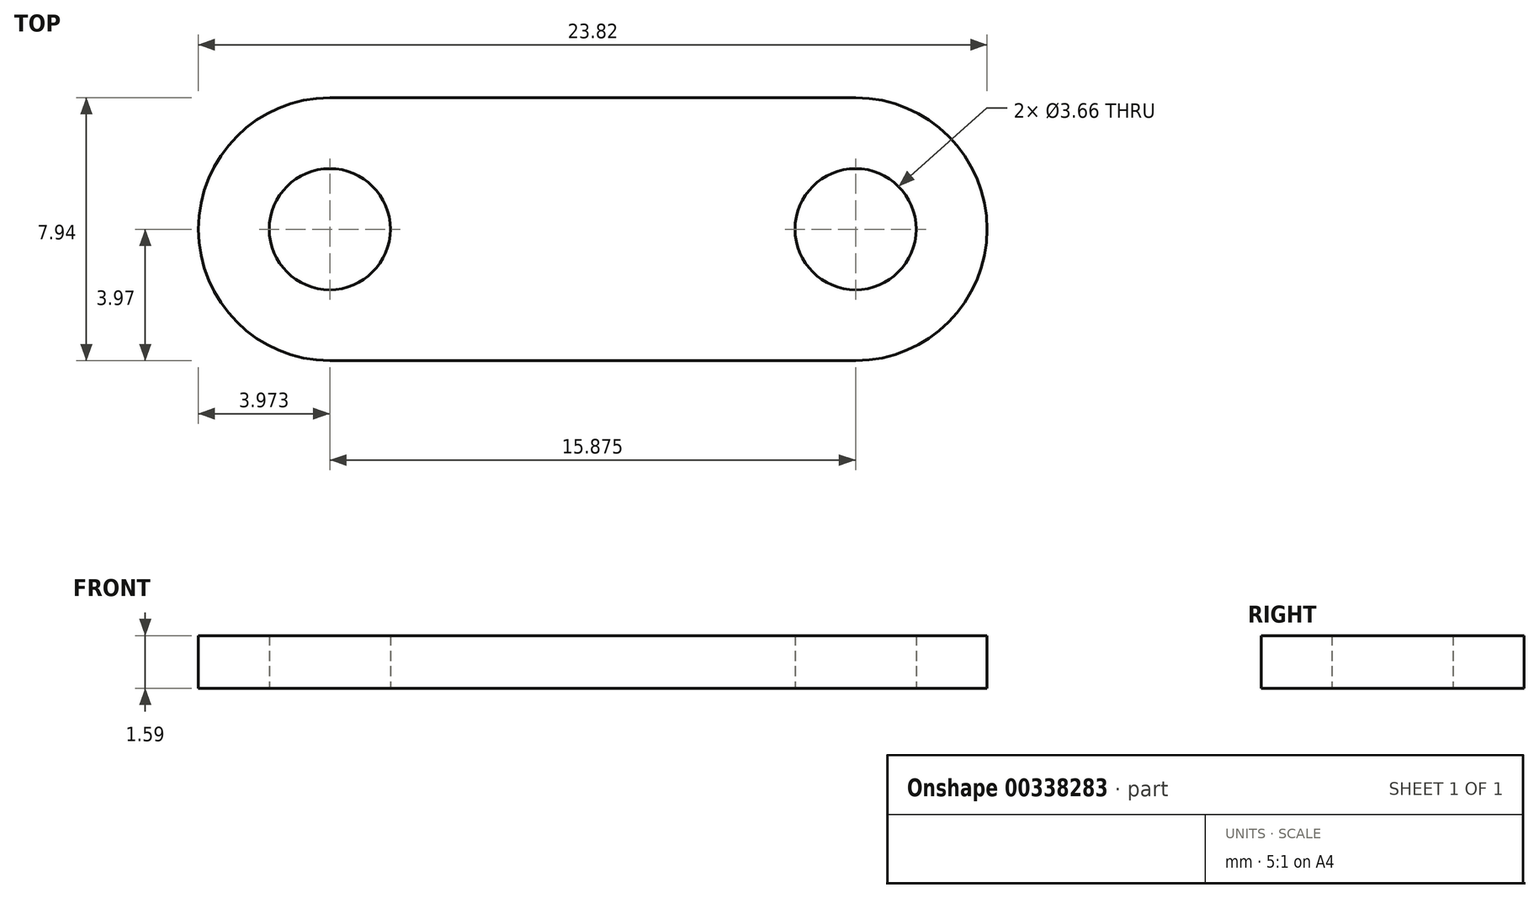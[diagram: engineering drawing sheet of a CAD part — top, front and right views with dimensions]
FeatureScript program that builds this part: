
annotation { "Feature Type Name" : "Feature", "Feature Type Description" : "" }
export const myFeature = defineFeature(function(context is Context, id is Id, definition is map)
    precondition{}
    {
        {
            var Q0;
            Q0=qCreatedBy(makeId("Top.planeOp"),FACE);
            var sketch = newSketch(context, id + "F0", { "sketchPlane" : qUnion([Q0])});
            skLineSegment(sketch, "E0.bottom", {"start": v(7.94, -3.97) * mm, "end": v(-7.94, -3.97) * mm});
            skLineSegment(sketch, "E0.top", {"start": v(7.94, 3.97) * mm, "end": v(-7.94, 3.97) * mm});
            skLineSegment(sketch, "E0.left", {"start": v(7.94, -3.97) * mm, "end": v(7.94, 3.97) * mm, "construction": true});
            skLineSegment(sketch, "E0.right", {"start": v(-7.94, -3.97) * mm, "end": v(-7.94, 3.97) * mm, "construction": true});
            skPoint(sketch, "E0.middle", {"position": v(0, 0) * mm});
            skArc(sketch, "E1", {"start": v(-7.94, 3.97) * mm, "mid": v(-11.9, 0) * mm, "end": v(-7.94, -3.97) * mm});
            skArc(sketch, "E2", {"start": v(7.94, -3.97) * mm, "mid": v(11.9, 0) * mm, "end": v(7.94, 3.97) * mm});
            skCircle(sketch, "E3", {"center": v(-7.94, 0) * mm, "radius": 1.83 * mm});
            skCircle(sketch, "E4", {"center": v(7.94, 0) * mm, "radius": 1.83 * mm});
            skSolve(sketch);
        }
        {
            var Q0;
            Q0 = qSketchRegion(id + "F0", true);
            extrude(context, id + "F1", {"entities" : qUnion([Q0]), "depth" : 1.59 * mm});
        }
    });
